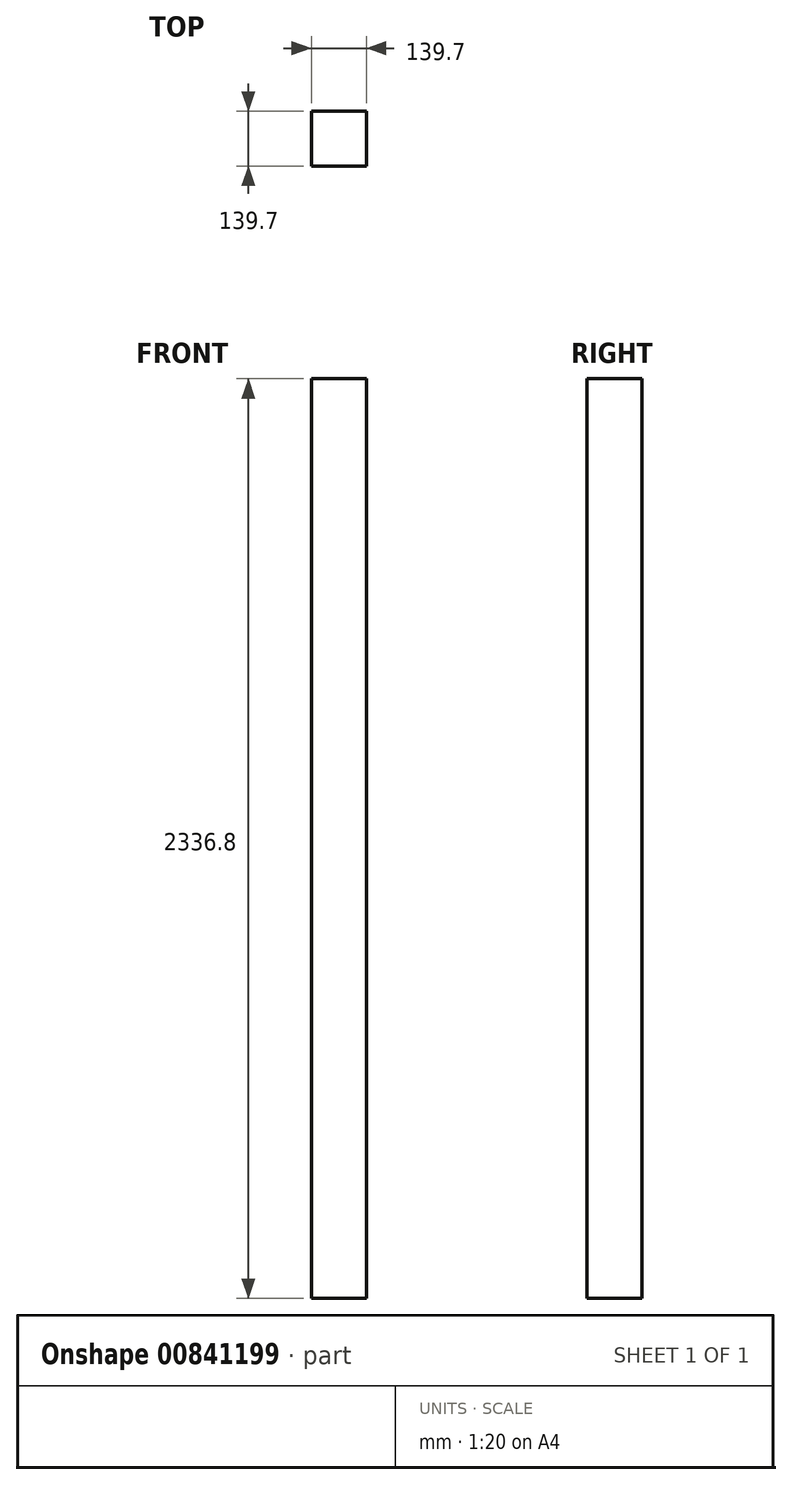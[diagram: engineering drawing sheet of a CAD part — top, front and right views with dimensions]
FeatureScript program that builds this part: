
annotation { "Feature Type Name" : "Feature", "Feature Type Description" : "" }
export const myFeature = defineFeature(function(context is Context, id is Id, definition is map)
    precondition{}
    {
        {
            var Q0;
            Q0=qCreatedBy(makeId("Top.planeOp"),FACE);
            var sketch = newSketch(context, id + "F0", { "sketchPlane" : qUnion([Q0])});
            skLineSegment(sketch, "E0.bottom", {"start": v(0, 0) * mm, "end": v(139.7, 0) * mm});
            skLineSegment(sketch, "E0.top", {"start": v(0, -139.7) * mm, "end": v(139.7, -139.7) * mm});
            skLineSegment(sketch, "E0.left", {"start": v(0, 0) * mm, "end": v(0, -139.7) * mm});
            skLineSegment(sketch, "E0.right", {"start": v(139.7, 0) * mm, "end": v(139.7, -139.7) * mm});
            skSolve(sketch);
        }
        {
            var Q0;
            Q0 = qSketchRegion(id + "F0", true);
            extrude(context, id + "F1", {"entities" : qUnion([Q0]), "depth" : 2336.8 * mm, "offsetDistance" : 25.4 * mm});
        }
    });
